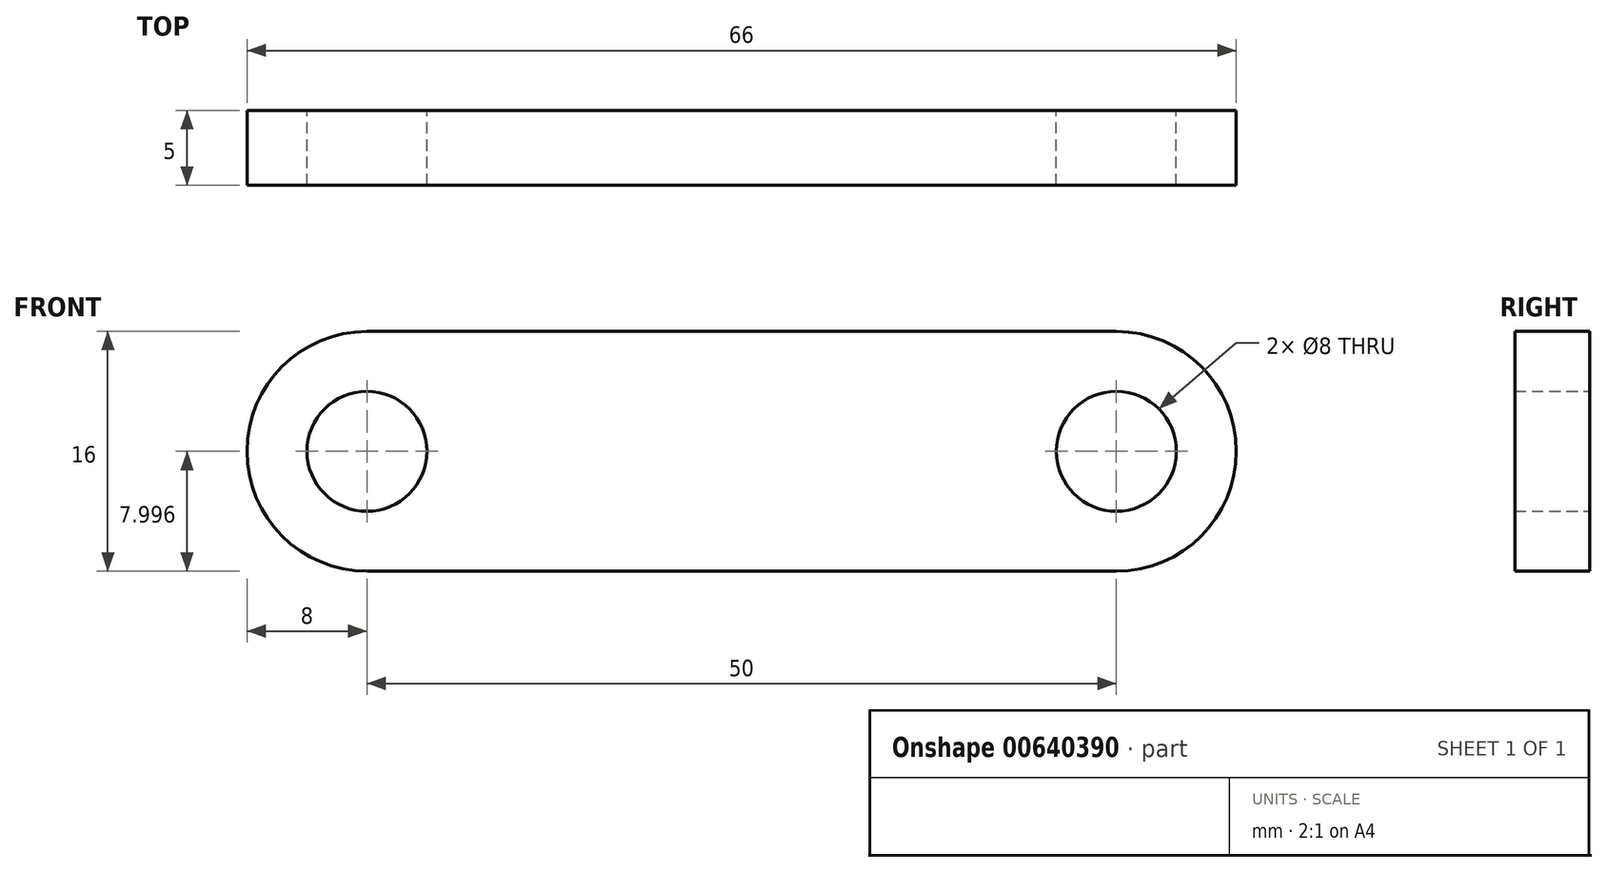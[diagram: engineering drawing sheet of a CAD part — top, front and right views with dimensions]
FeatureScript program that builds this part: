
annotation { "Feature Type Name" : "Feature", "Feature Type Description" : "" }
export const myFeature = defineFeature(function(context is Context, id is Id, definition is map)
    precondition{}
    {
        {
            var Q0;
            Q0=qCreatedBy(makeId("Front.planeOp"),FACE);
            var sketch = newSketch(context, id + "F0", { "sketchPlane" : qUnion([Q0])});
            skLineSegment(sketch, "E0.bottom", {"start": v(-25, 8.46) * mm, "end": v(0, 8.46) * mm});
            skLineSegment(sketch, "E0.top", {"start": v(-25, -7.54) * mm, "end": v(0, -7.54) * mm});
            skLineSegment(sketch, "E0.right", {"start": v(0, 8.46) * mm, "end": v(0, -7.54) * mm});
            skArc(sketch, "E1", {"start": v(-25, 8.46) * mm, "mid": v(-33, 0.46) * mm, "end": v(-25, -7.54) * mm});
            skCircle(sketch, "E2", {"center": v(-25, 0.46) * mm, "radius": 4 * mm});
            skSolve(sketch);
        }
        {
            var Q0;
            Q0=makeQuery(id+"F0.imprint","IMPRINT",FACE,{"disambiguationData":[TD([[makeQuery(id+"F0.imprint","IMPRINT",EDGE,{"derivedFrom":sQuery(id+"F0.wireOp",EDGE,"E0.bottom")}),-1.0]])]});
            extrude(context, id + "F1", {"entities" : qUnion([Q0]), "endBound" : BoundingType.SYMMETRIC, "depth" : 5 * mm, "offsetDistance" : 25 * mm});
        }
        {
            var Q0;
            Q0=makeQuery(id+"F1.opExtrude","SWEPT_BODY",BODY,{"disambiguationData":[OSD([sQuery(id+"F0.wireOp",EDGE,"E0.bottom"),sQuery(id+"F0.wireOp",EDGE,"E0.top"),sQuery(id+"F0.wireOp",EDGE,"E0.right"),sQuery(id+"F0.wireOp",EDGE,"E1"),sQuery(id+"F0.wireOp",EDGE,"E2")])]});
            var Q1;
            Q1=makeQuery(id+"F1.opExtrude","SWEPT_FACE",FACE,{"disambiguationData":[OSD([sQuery(id+"F0.wireOp",EDGE,"E0.right")])]});
            mirror(context, id + "F2", {"operationType" : NewBodyOperationType.ADD, "entities" : qUnion([Q0]), "mirrorPlane" : qUnion([Q1])});
        }
    });
